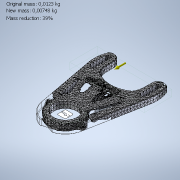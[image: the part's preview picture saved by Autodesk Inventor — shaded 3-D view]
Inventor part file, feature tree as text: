
AUTODESK INVENTOR PART (.ipt)
format: ipt  version: 2020.1 (Build 241239000, 239)  size: 7,220,224 bytes
history: native  units: mm
features: thread x3, sketch x3, emboss x2, fillet x2, extrude x1, chamfer x1, other x1
ambient origin geometry x8: Origin, YZ Plane, XZ Plane, XY Plane, X Axis, Y Axis, Z Axis, Center Point
bodies: Body1 (feature_tree)
feature tree (13):
  extrude  "Extrusion3"  Depth=20.0mm
  thread  "Thread1"  [1 undecoded]
  thread  "Thread2"  [1 undecoded]
  thread  "Thread3"  [1 undecoded]
  emboss  "Emboss1"
  emboss  "Emboss2"
  fillet  "Fillet3"  Radius=3.5mm
  fillet  "Fillet5"  Radius=32.0mm
  chamfer  "Chamfer3"  Distance=3.0mm
  other  "Center Lines"
  sketch  "Sketch1"  dims[d0=51.5mm d1=20.0mm d3=3.5mm d4=3.5mm d5=7.0mm d9=3.5mm d11=32.0mm]
  sketch  "Sketch3"  dims[d15=4.1mm]
  sketch  "Sketch4"  dims[d24=3.0mm d25=3.0mm d27=45.0deg d29=3.0mm d30=3.0mm d40=5.5mm d41=0.0mm d44=10.0mm d45=0.0mm d46=10.0mm d47=0.0mm d48=10.0mm d49=0.0mm d50=10.0mm d51=52.0mm d53=27.0mm d65=0.2mm d66=0.0mm d67=2.0mm d68=2.0mm d69=5.0mm d70=25.0mm d71=5.0mm d72=25.0mm d73=0.2mm d74=0.0mm d75=80.75mm d76=7.5mm d77=3.75mm d81=6.25mm d82=12.5mm d85=5.0mm d86=4.0mm d91=0.5mm d94=2.0mm d95=0.5mm d96=2.0mm d97=45.0deg d98=15.0deg d99=24.0mm d102=43.0mm d103=2.0mm d109=7.0mm d110=7.0mm d113=3.332mm d115=42.484mm]
note: 3 required parameter values undecoded (feature->parameter linkage not recoverable at this tier; creation-order binding heuristic only, values carry confidence <= 0.55)
